# Revit family: 17L-CC
name_source: partatom
category: Lighting Fixtures
units: mm (PartAtom-declared; Revit-internal decimal feet)

## family parameters
Cut with Voids When Loaded = No
Host = Face
Light Source = Yes
OmniClass Number = 23.80.70.11.14.17
OmniClass Title = Direct/Indirect
Part Type = Normal
Room Calculation Point = No
Round Connector Dimension = Use Diameter
Shared = Yes

## types (3) — shared parameters
Apparent Load = 4 VA
Assembly Code = D5020200
Backbox = Paint - Matte White
Circuiting = 1 Circuit
Color Filter = 16777215
Default Elevation = 48 "
Description = Indirect Light Coves by Armstrong
Dimming Lamp Color Temperature Shift = <None>
Emit Shape Visible in Rendering = No
Emit from Rectangle Length = 1.5 "
Glass = White Glass
Lamp = LED
Load Classification = Lighting
Manufacturer = Litecontrol
Model = 17L-CC
Mounting = Armstrong Axiom Cove Ceiling
Nominal Watts = 4 W
Photometric Notes = More IES files download on Photometric Link
Photometric Web File = 17L-CC-AI-02-C1-35K-I030.IES
Power Factor = 1
Tilt Angle = 90.00°
Type Comments = Lighting Fixture
URL = https://www.currentlighting.com
Voltage = 120 V
Warranty = 5 years warranty
Wattage Comments = 133 Lumens/Watt

## per-type parameters (varying)
| type | Emit from Rectangle Width | zz Length 1 |
| 17L-CC-02 | 23.813 " | 24.063 " |
| 17L-CC-03 | 35.75 " | 36 " |
| 17L-CC-04 | 47.75 " | 48 " |

## geometry (parser evidence)
native form markers: Sweep x4
no freeform markers — native parametric forms only
